FCSTD DOCUMENT  (FreeCAD 0.19R24267 +148 (Git))
Label: Master Sketch 2
License: All rights reserved
LicenseURL: http://en.wikipedia.org/wiki/All_rights_reserved
objects: Sketcher::SketchObject×1, PartDesign::Body×1
note: 2 computed .brp shape members not serialized (recipe doc carries the construction recipe); baked Part::Feature solids carry a one-line shape summary decoded from their .brp

FEATURE [Sketcher::SketchObject] Sketch
  FullyConstrained = false
  MapMode = 5
  Support = -> [XY_Plane]
  sketch-geometry (21):
    g0: Circle CenterX=70.8621 CenterY=65.4424 CenterZ=0 NormalX=0 NormalY=0 NormalZ=1 AngleXU=0 Radius=50
    g1: Circle CenterX=70.8621 CenterY=65.4424 CenterZ=0 NormalX=0 NormalY=0 NormalZ=1 AngleXU=0 Radius=20
    g2: LineSegment StartX=38.3126 StartY=90.2703 StartZ=0 EndX=103.313 EndY=90.2703 EndZ=0
    g3: LineSegment StartX=103.313 StartY=90.2703 StartZ=0 EndX=103.313 EndY=40.2703 EndZ=0
    g4: LineSegment StartX=103.313 StartY=40.2703 StartZ=0 EndX=38.3126 EndY=40.2703 EndZ=0
    g5: LineSegment StartX=38.3126 StartY=40.2703 StartZ=0 EndX=38.3126 EndY=90.2703 EndZ=0
    g6: LineSegment StartX=-172.168 StartY=15.5646 StartZ=0 EndX=-132.168 EndY=15.5646 EndZ=0
    g7: LineSegment StartX=-132.168 StartY=15.5646 StartZ=0 EndX=-132.168 EndY=115.565 EndZ=0
    g8: LineSegment StartX=-132.168 StartY=115.565 StartZ=0 EndX=-172.168 EndY=115.565 EndZ=0
    g9: LineSegment StartX=-172.168 StartY=115.565 StartZ=0 EndX=-172.168 EndY=15.5646 EndZ=0
    g10: LineSegment StartX=70.8621 StartY=65.4424 StartZ=0 EndX=-172.168 EndY=65.4424 EndZ=0
    g11: LineSegment StartX=-132.168 StartY=90.2703 StartZ=0 EndX=-32.1682 EndY=90.2703 EndZ=0
    g12: LineSegment StartX=-32.1682 StartY=90.2703 StartZ=0 EndX=-32.1682 EndY=40.2703 EndZ=0
    g13: LineSegment StartX=-32.1682 StartY=40.2703 StartZ=0 EndX=-132.168 EndY=40.2703 EndZ=0
    g14: LineSegment StartX=-132.168 StartY=40.2703 StartZ=0 EndX=-132.168 EndY=90.2703 EndZ=0
    g15: LineSegment StartX=-32.1682 StartY=85.4158 StartZ=0 EndX=12.8318 EndY=85.4158 EndZ=0
    g16: LineSegment StartX=12.8318 StartY=85.4158 StartZ=0 EndX=12.8318 EndY=45.4505 EndZ=0
    g17: LineSegment StartX=12.8318 StartY=45.4505 StartZ=0 EndX=-32.1682 EndY=45.4505 EndZ=0
    g18: LineSegment StartX=-32.1682 StartY=45.4505 StartZ=0 EndX=-32.1682 EndY=85.4158 EndZ=0
    g19: GeomPoint X=69.8318 Y=85.4158 Z=0
    g20: GeomPoint X=70.2906 Y=45.4505 Z=0
  constraints (52):
    c: Coincident(g1,g0)
    c: Diameter(g0) = 100
    c: Diameter(g1) = 40
    c: Coincident(g2,g3)
    c: Coincident(g3,g4)
    c: Coincident(g4,g5)
    c: Coincident(g5,g2)
    c: Horizontal(g2)
    c: Horizontal(g4)
    c: Vertical(g3)
    c: Vertical(g5)
    c: DistanceY(g3,g3) = 50
    c: DistanceX(g2,g2) = 65
    c: Coincident(g6,g7)
    c: Coincident(g7,g8)
    c: Coincident(g8,g9)
    c: Coincident(g9,g6)
    c: Horizontal(g6)
    c: Horizontal(g8)
    c: Vertical(g7)
    c: Vertical(g9)
    c: DistanceX(g8,g8) = 40
    c: DistanceY(g7,g7) = 100
    c: Coincident(g10,g0)
    c: PointOnObject(g10,g9)
    c: Horizontal(g10)
    c: Coincident(g11,g12)
    c: Coincident(g12,g13)
    c: Coincident(g13,g14)
    c: Coincident(g14,g11)
    c: Horizontal(g11)
    c: Horizontal(g13)
    c: Vertical(g12)
    c: Vertical(g14)
    c: PointOnObject(g11,g7)
    c: DistanceY(g12,g12) = 50
    c: Horizontal(g11,g2)
    c: DistanceX(g11,g11) = 100
    c: Coincident(g15,g16)
    c: Coincident(g16,g17)
    c: Coincident(g17,g18)
    c: Coincident(g18,g15)
    c: Horizontal(g15)
    c: Horizontal(g17)
    c: Vertical(g16)
    c: Vertical(g18)
    c: PointOnObject(g15,g12)
    c: PointOnObject(g19,g1)
    c: PointOnObject(g20,g1)
    c: Horizontal(g15,g19)
    c: Horizontal(g16,g20)
    c: DistanceX(g15,g15) = 45
FEATURE [PartDesign::Body] Body
  Group = -> [Sketch]
  Origin = -> Origin
